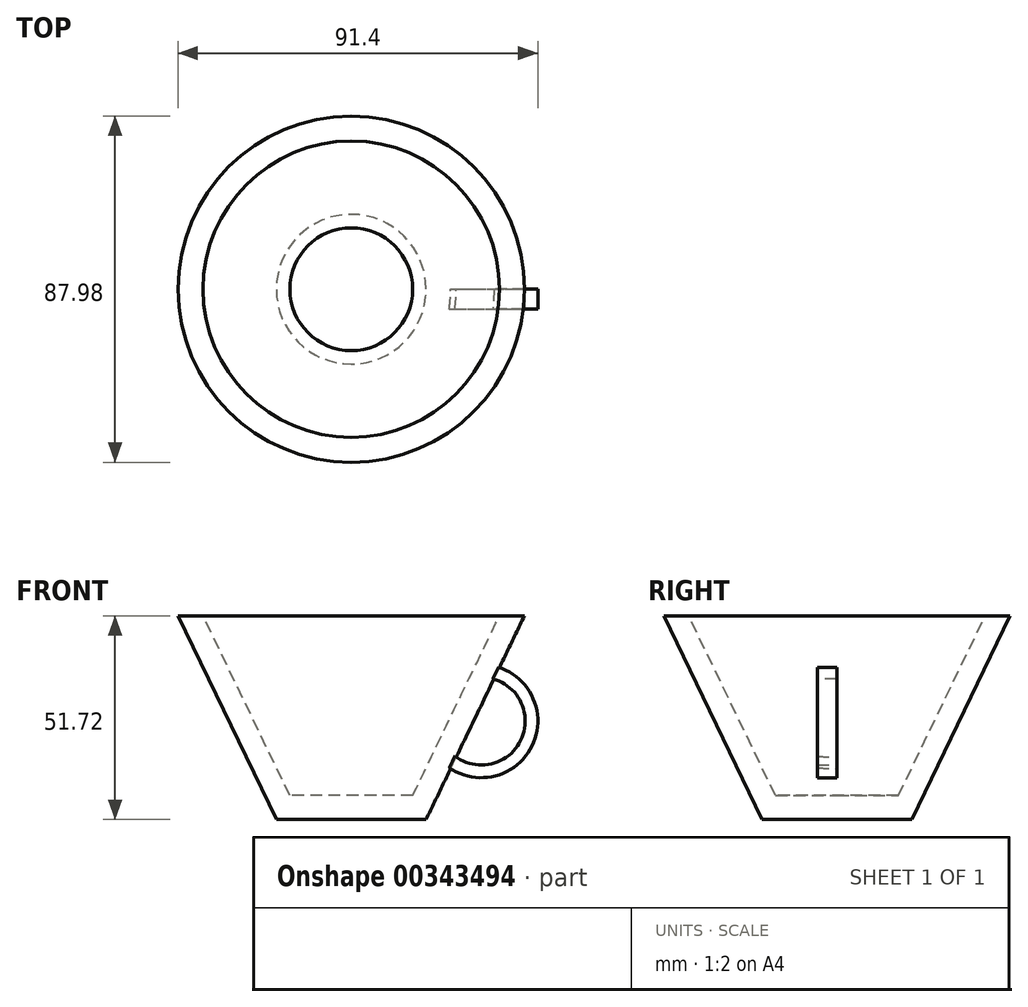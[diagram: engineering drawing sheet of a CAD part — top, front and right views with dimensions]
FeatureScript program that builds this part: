
annotation { "Feature Type Name" : "Feature", "Feature Type Description" : "" }
export const myFeature = defineFeature(function(context is Context, id is Id, definition is map)
    precondition{}
    {
        {
            var Q0;
            Q0=qCreatedBy(makeId("Front.planeOp"),FACE);
            var sketch = newSketch(context, id + "F0", { "sketchPlane" : qUnion([Q0])});
            skLineSegment(sketch, "E0", {"start": v(0, 0) * mm, "end": v(19.02, 0) * mm});
            skLineSegment(sketch, "E1", {"start": v(19.02, 0) * mm, "end": v(43.99, 51.72) * mm});
            skLineSegment(sketch, "E2", {"start": v(43.99, 51.72) * mm, "end": v(37.65, 51.72) * mm});
            skLineSegment(sketch, "E3", {"start": v(37.65, 51.72) * mm, "end": v(15.6, 6.05) * mm});
            skLineSegment(sketch, "E4", {"start": v(15.6, 6.05) * mm, "end": v(0, 6.05) * mm});
            skLineSegment(sketch, "E5", {"start": v(0, 6.05) * mm, "end": v(0, 0) * mm});
            skSolve(sketch);
        }
        {
            var Q0;
            Q0 = qSketchRegion(id + "F0", true);
            var Q1;
            Q1=sQuery(id+"F0.wireOp",EDGE,"E5");
            revolve(context, id + "F1", {"entities" : qUnion([Q0]), "axis" : qUnion([Q1]), "revolveType" : RevolveType.FULL});
        }
        {
            var Q0;
            Q0=qCreatedBy(makeId("Front.planeOp"),FACE);
            var sketch = newSketch(context, id + "F2", { "sketchPlane" : qUnion([Q0])});
            skArc(sketch, "E6", {"start": v(24.36, 13.53) * mm, "mid": v(45.98, 18.72) * mm, "end": v(36.62, 38.89) * mm});
            skArc(sketch, "E7", {"start": v(25.83, 16.47) * mm, "mid": v(43.04, 20.03) * mm, "end": v(35.42, 35.87) * mm});
            skLineSegment(sketch, "E8", {"start": v(36.62, 38.89) * mm, "end": v(35.42, 35.87) * mm});
            skLineSegment(sketch, "E9", {"start": v(25.83, 16.47) * mm, "end": v(24.36, 13.53) * mm});
            skSolve(sketch);
        }
        {
            var Q0;
            Q0 = qSketchRegion(id + "F2", true);
            extrude(context, id + "F3", {"entities" : qUnion([Q0]), "operationType" : NewBodyOperationType.ADD, "depth" : 5 * mm});
        }
    });
